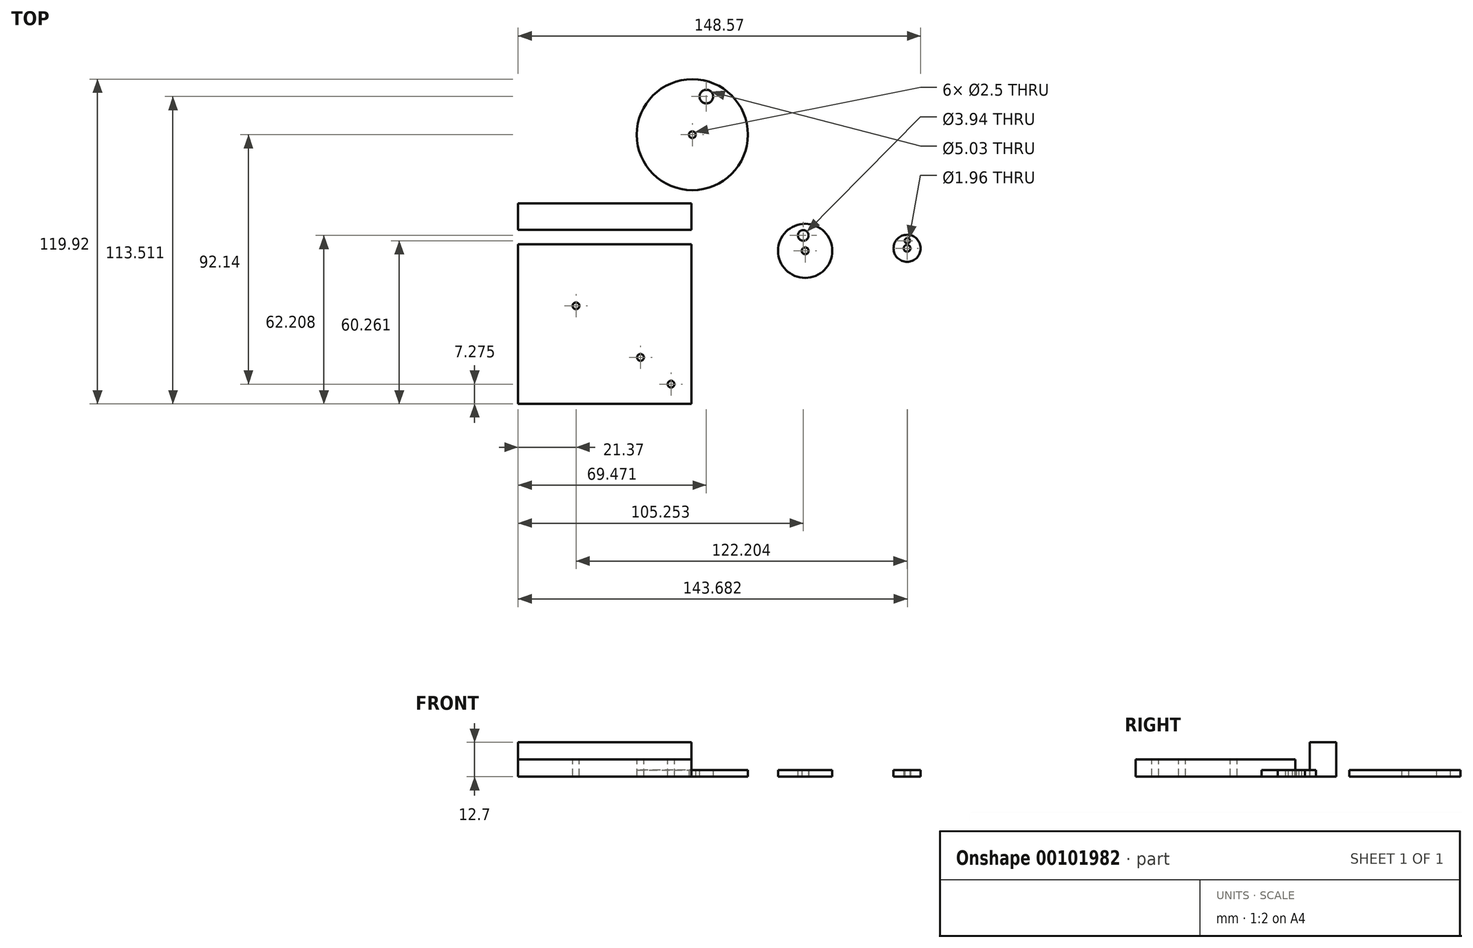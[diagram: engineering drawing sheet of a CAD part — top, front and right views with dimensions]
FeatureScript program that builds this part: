
annotation { "Feature Type Name" : "Feature", "Feature Type Description" : "" }
export const myFeature = defineFeature(function(context is Context, id is Id, definition is map)
    precondition{}
    {
        {
            var Q0;
            Q0=qCreatedBy(makeId("Top.planeOp"),FACE);
            var sketch = newSketch(context, id + "F0", { "sketchPlane" : qUnion([Q0])});
            skCircle(sketch, "E0", {"center": v(-45.77, 49.57) * mm, "radius": 20.5 * mm});
            skCircle(sketch, "E1", {"center": v(-40.6, 63.66) * mm, "radius": 2.51 * mm});
            skSolve(sketch);
        }
        {
            var Q0;
            Q0=qCreatedBy(makeId("Top.planeOp"),FACE);
            var sketch = newSketch(context, id + "F1", { "sketchPlane" : qUnion([Q0])});
            skCircle(sketch, "E2", {"center": v(-4.12, 6.67) * mm, "radius": 10 * mm});
            skCircle(sketch, "E3", {"center": v(33.5, 7.6) * mm, "radius": 5 * mm});
            skCircle(sketch, "E4", {"center": v(-4.83, 12.36) * mm, "radius": 1.97 * mm});
            skCircle(sketch, "E5", {"center": v(33.6, 10.41) * mm, "radius": 0.98 * mm});
            skSolve(sketch);
        }
        {
            var Q0;
            Q0 = qSketchRegion(id + "F1", true);
            var Q1;
            Q1=makeQuery(id+"F0.imprint","IMPRINT",FACE,{"disambiguationData":[TD([[makeQuery(id+"F0.imprint","IMPRINT",EDGE,{"derivedFrom":sQuery(id+"F0.wireOp",EDGE,"E0")}),1.0]])]});
            extrude(context, id + "F2", {"entities" : qUnion([Q0, Q1]), "depth" : 2.5 * mm});
        }
        {
            var Q0;
            Q0=qCreatedBy(makeId("Top.planeOp"),FACE);
            var sketch = newSketch(context, id + "F3", { "sketchPlane" : qUnion([Q0])});
            skLineSegment(sketch, "E6.bottom", {"start": v(-110.08, 9.07) * mm, "end": v(-46.05, 9.07) * mm});
            skLineSegment(sketch, "E6.top", {"start": v(-110.08, -49.85) * mm, "end": v(-46.05, -49.85) * mm});
            skLineSegment(sketch, "E6.left", {"start": v(-110.08, 9.07) * mm, "end": v(-110.08, -49.85) * mm});
            skLineSegment(sketch, "E6.right", {"start": v(-46.05, 9.07) * mm, "end": v(-46.05, -49.85) * mm});
            skLineSegment(sketch, "E7.bottom", {"start": v(-110.08, 14.38) * mm, "end": v(-46.05, 14.38) * mm});
            skLineSegment(sketch, "E7.top", {"start": v(-110.08, 24.22) * mm, "end": v(-46.05, 24.22) * mm});
            skLineSegment(sketch, "E7.left", {"start": v(-110.08, 14.38) * mm, "end": v(-110.08, 24.22) * mm});
            skLineSegment(sketch, "E7.right", {"start": v(-46.05, 14.38) * mm, "end": v(-46.05, 24.22) * mm});
            skSolve(sketch);
        }
        {
            var Q0;
            Q0 = qSketchRegion(id + "F3", true);
            extrude(context, id + "F4", {"entities" : qUnion([Q0]), "depth" : 6.35 * mm});
        }
        {
            var Q0;
            Q0=makeQuery(id+"F4.opExtrude","CAP_FACE",FACE,{"disambiguationData":[OSD([sQuery(id+"F3.wireOp",EDGE,"E7.bottom"),sQuery(id+"F3.wireOp",EDGE,"E7.top"),sQuery(id+"F3.wireOp",EDGE,"E7.left"),sQuery(id+"F3.wireOp",EDGE,"E7.right")])],"isStart":false});
            extrude(context, id + "F5", {"entities" : qUnion([Q0]), "operationType" : NewBodyOperationType.ADD, "depth" : 6.35 * mm});
        }
        {
            var Q0;
            Q0=sQuery(id+"F0.wireOp",VERTEX,"E0.center");
            var Q1;
            Q1=makeQuery(id+"F2.opExtrude","SWEPT_BODY",BODY,{"disambiguationData":[OSD([sQuery(id+"F0.wireOp",EDGE,"E0")])]});
            hole(context, id + "F6", {"style" : HoleStyle.SIMPLE, "endStyle" : HoleEndStyle.THROUGH, "oppositeDirection" : true, "holeDiameter" : 2.5 * mm, "locations" : qUnion([Q0]), "scope" : qUnion([Q1]), "isTappedThrough" : true});
        }
        {
            var Q0;
            Q0=makeQuery(id+"F4.opExtrude","CAP_FACE",FACE,{"disambiguationData":[OSD([sQuery(id+"F3.wireOp",EDGE,"E6.bottom"),sQuery(id+"F3.wireOp",EDGE,"E6.top"),sQuery(id+"F3.wireOp",EDGE,"E6.left"),sQuery(id+"F3.wireOp",EDGE,"E6.right")])],"isStart":false});
            var sketch = newSketch(context, id + "F7", { "sketchPlane" : qUnion([Q0])});
            skCircle(sketch, "E8", {"center": v(-88.71, -13.63) * mm, "radius": 20.5 * mm});
            skCircle(sketch, "E9", {"center": v(-64.9, -32.69) * mm, "radius": 10 * mm});
            skCircle(sketch, "E10", {"center": v(-53.62, -42.57) * mm, "radius": 5 * mm});
            skSolve(sketch);
        }
        {
            var Q0;
            Q0=sQuery(id+"F7.wireOp",VERTEX,"E8.center");
            var Q1;
            Q1=makeQuery(id+"F4.opExtrude","SWEPT_BODY",BODY,{"disambiguationData":[OSD([sQuery(id+"F3.wireOp",EDGE,"E6.bottom"),sQuery(id+"F3.wireOp",EDGE,"E6.top"),sQuery(id+"F3.wireOp",EDGE,"E6.left"),sQuery(id+"F3.wireOp",EDGE,"E6.right")])]});
            hole(context, id + "F8", {"style" : HoleStyle.SIMPLE, "endStyle" : HoleEndStyle.THROUGH, "holeDiameter" : 2.5 * mm, "locations" : qUnion([Q0]), "scope" : qUnion([Q1]), "isTappedThrough" : true});
        }
        {
            var Q0;
            Q0=sQuery(id+"F7.wireOp",VERTEX,"E9.center");
            var Q1;
            Q1=sQuery(id+"F7.wireOp",VERTEX,"E10.center");
            var Q2;
            Q2=sQuery(id+"F1.wireOp",VERTEX,"E2.center");
            var Q3;
            Q3=sQuery(id+"F1.wireOp",VERTEX,"E3.center");
            var Q4;
            Q4=makeQuery(id+"F4.opExtrude","SWEPT_BODY",BODY,{"disambiguationData":[OSD([sQuery(id+"F3.wireOp",EDGE,"E6.bottom"),sQuery(id+"F3.wireOp",EDGE,"E6.top"),sQuery(id+"F3.wireOp",EDGE,"E6.left"),sQuery(id+"F3.wireOp",EDGE,"E6.right")])]});
            hole(context, id + "F9", {"style" : HoleStyle.SIMPLE, "endStyle" : HoleEndStyle.THROUGH, "holeDiameter" : 2.5 * mm, "locations" : qUnion([Q0, Q1, Q2, Q3]), "scope" : qUnion([Q4]), "isTappedThrough" : true});
        }
        {
            var Q0;
            Q0=sQuery(id+"F1.wireOp",VERTEX,"E2.center");
            var Q1;
            Q1=sQuery(id+"F1.wireOp",VERTEX,"E3.center");
            var Q2;
            Q2=makeQuery(id+"F2.opExtrude","SWEPT_BODY",BODY,{"disambiguationData":[OSD([sQuery(id+"F1.wireOp",EDGE,"E2")])]});
            var Q3;
            Q3=makeQuery(id+"F2.opExtrude","SWEPT_BODY",BODY,{"disambiguationData":[OSD([sQuery(id+"F1.wireOp",EDGE,"E3")])]});
            hole(context, id + "F10", {"style" : HoleStyle.SIMPLE, "endStyle" : HoleEndStyle.THROUGH, "oppositeDirection" : true, "holeDiameter" : 2.5 * mm, "locations" : qUnion([Q0, Q1]), "scope" : qUnion([Q2, Q3]), "isTappedThrough" : true});
        }
    });
